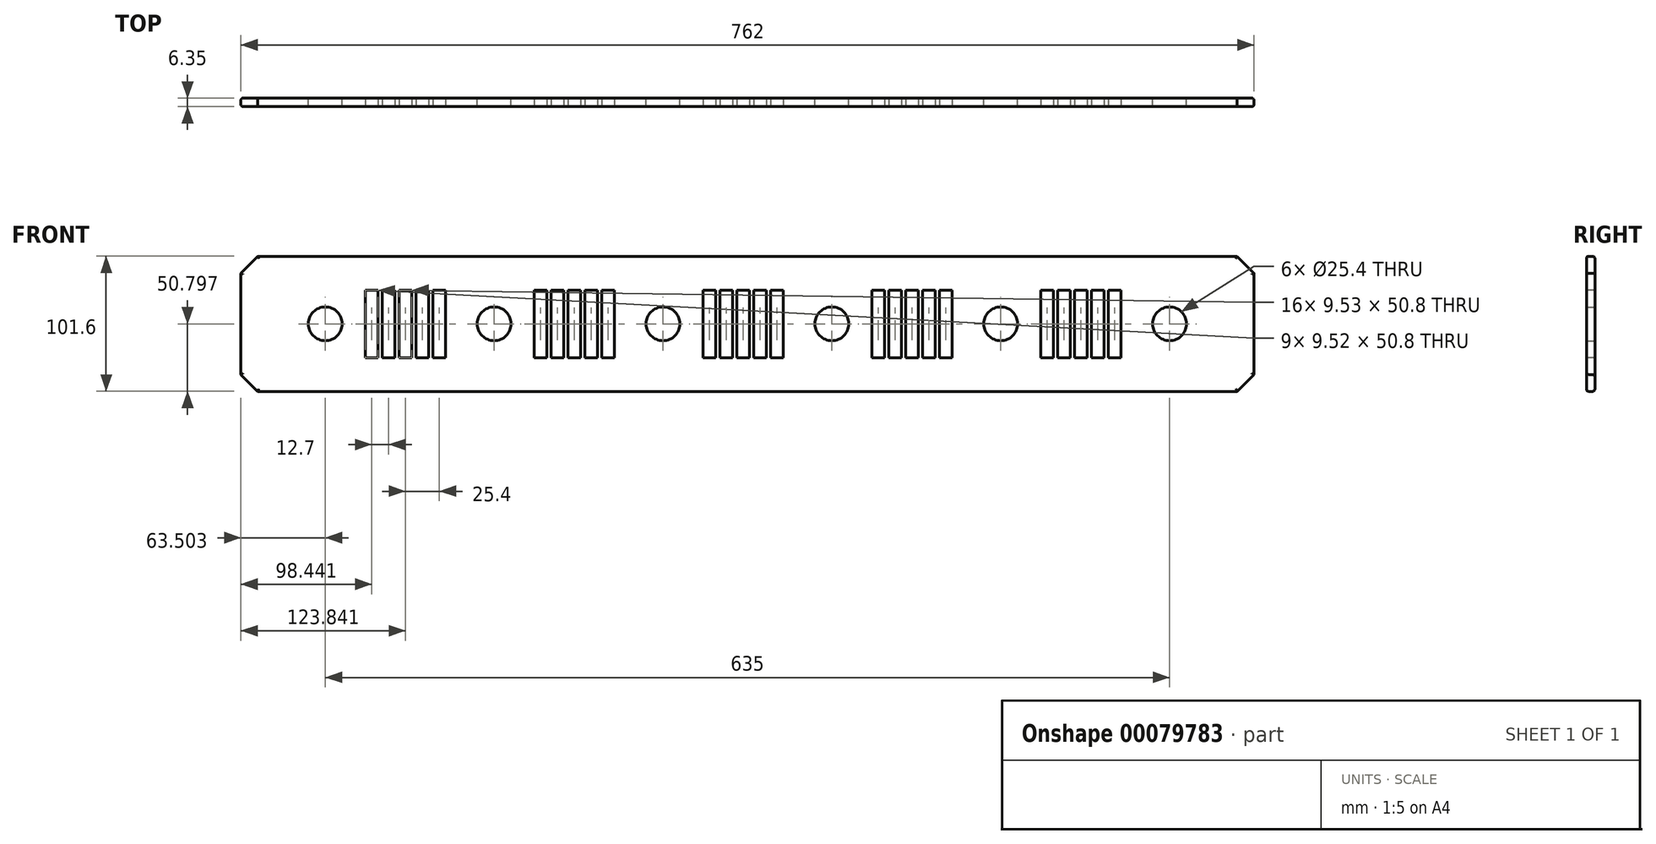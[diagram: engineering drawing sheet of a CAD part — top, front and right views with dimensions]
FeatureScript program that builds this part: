
annotation { "Feature Type Name" : "Feature", "Feature Type Description" : "" }
export const myFeature = defineFeature(function(context is Context, id is Id, definition is map)
    precondition{}
    {
        {
            var Q0;
            Q0=qCreatedBy(makeId("Front.planeOp"),FACE);
            var sketch = newSketch(context, id + "F0", { "sketchPlane" : qUnion([Q0])});
            skLineSegment(sketch, "E0.bottom", {"start": v(-378.92, -35.34) * mm, "end": v(383.08, -35.34) * mm});
            skLineSegment(sketch, "E0.top", {"start": v(-378.92, -136.94) * mm, "end": v(383.08, -136.94) * mm});
            skLineSegment(sketch, "E0.left", {"start": v(-378.92, -35.34) * mm, "end": v(-378.92, -136.94) * mm});
            skLineSegment(sketch, "E0.right", {"start": v(383.08, -35.34) * mm, "end": v(383.08, -136.94) * mm});
            skCircle(sketch, "E1", {"center": v(-315.42, -86.14) * mm, "radius": 12.7 * mm});
            skPoint(sketch, "E1.centerSnap0", {"position": v(-378.92, -86.14) * mm});
            skCircle(sketch, "E2", {"center": v(-188.42, -86.14) * mm, "radius": 12.7 * mm});
            skCircle(sketch, "E3", {"center": v(-61.42, -86.14) * mm, "radius": 12.7 * mm});
            skCircle(sketch, "E4", {"center": v(65.58, -86.14) * mm, "radius": 12.7 * mm});
            skCircle(sketch, "E5", {"center": v(192.58, -86.14) * mm, "radius": 12.7 * mm});
            skCircle(sketch, "E6", {"center": v(319.58, -86.14) * mm, "radius": 12.7 * mm});
            skSolve(sketch);
        }
        {
            var Q0;
            Q0=makeQuery(id+"F0.imprint","IMPRINT",FACE,{"disambiguationData":[TD([[makeQuery(id+"F0.imprint","IMPRINT",EDGE,{"derivedFrom":sQuery(id+"F0.wireOp",EDGE,"E0.bottom")}),-1.0]])]});
            extrude(context, id + "F1", {"entities" : qUnion([Q0]), "depth" : 6.35 * mm});
        }
        {
            var Q0;
            Q0=makeQuery(id+"F1.opExtrude","CAP_FACE",FACE,{"disambiguationData":[OSD([sQuery(id+"F0.wireOp",EDGE,"E0.bottom"),sQuery(id+"F0.wireOp",EDGE,"E0.top"),sQuery(id+"F0.wireOp",EDGE,"E0.left"),sQuery(id+"F0.wireOp",EDGE,"E0.right"),sQuery(id+"F0.wireOp",EDGE,"E1"),sQuery(id+"F0.wireOp",EDGE,"E2"),sQuery(id+"F0.wireOp",EDGE,"E3"),sQuery(id+"F0.wireOp",EDGE,"E4"),sQuery(id+"F0.wireOp",EDGE,"E5"),sQuery(id+"F0.wireOp",EDGE,"E6")])],"isStart":false});
            var sketch = newSketch(context, id + "F2", { "sketchPlane" : qUnion([Q0])});
            skLineSegment(sketch, "E7.bottom", {"start": v(-285.24, -60.74) * mm, "end": v(-275.72, -60.74) * mm});
            skLineSegment(sketch, "E7.top", {"start": v(-285.24, -111.54) * mm, "end": v(-275.72, -111.54) * mm});
            skLineSegment(sketch, "E7.left", {"start": v(-285.24, -60.74) * mm, "end": v(-285.24, -111.54) * mm});
            skLineSegment(sketch, "E7.right", {"start": v(-275.72, -60.74) * mm, "end": v(-275.72, -111.54) * mm});
            skLineSegment(sketch, "E8.1.0.0", {"start": v(-272.54, -60.74) * mm, "end": v(-263.02, -60.74) * mm});
            skLineSegment(sketch, "E8.1.0.1", {"start": v(-272.54, -111.54) * mm, "end": v(-263.02, -111.54) * mm});
            skLineSegment(sketch, "E8.1.0.2", {"start": v(-263.02, -60.74) * mm, "end": v(-263.02, -111.54) * mm});
            skLineSegment(sketch, "E8.1.0.3", {"start": v(-272.54, -60.74) * mm, "end": v(-272.54, -111.54) * mm});
            skLineSegment(sketch, "E8.2.0.0", {"start": v(-259.84, -60.74) * mm, "end": v(-250.32, -60.74) * mm});
            skLineSegment(sketch, "E8.2.0.1", {"start": v(-259.84, -111.54) * mm, "end": v(-250.32, -111.54) * mm});
            skLineSegment(sketch, "E8.2.0.2", {"start": v(-250.32, -60.74) * mm, "end": v(-250.32, -111.54) * mm});
            skLineSegment(sketch, "E8.2.0.3", {"start": v(-259.84, -60.74) * mm, "end": v(-259.84, -111.54) * mm});
            skLineSegment(sketch, "E8.3.0.0", {"start": v(-247.14, -60.74) * mm, "end": v(-237.62, -60.74) * mm});
            skLineSegment(sketch, "E8.3.0.1", {"start": v(-247.14, -111.54) * mm, "end": v(-237.62, -111.54) * mm});
            skLineSegment(sketch, "E8.3.0.2", {"start": v(-237.62, -60.74) * mm, "end": v(-237.62, -111.54) * mm});
            skLineSegment(sketch, "E8.3.0.3", {"start": v(-247.14, -60.74) * mm, "end": v(-247.14, -111.54) * mm});
            skLineSegment(sketch, "E8.4.0.0", {"start": v(-234.44, -60.74) * mm, "end": v(-224.92, -60.74) * mm});
            skLineSegment(sketch, "E8.4.0.1", {"start": v(-234.44, -111.54) * mm, "end": v(-224.92, -111.54) * mm});
            skLineSegment(sketch, "E8.4.0.2", {"start": v(-224.92, -60.74) * mm, "end": v(-224.92, -111.54) * mm});
            skLineSegment(sketch, "E8.4.0.3", {"start": v(-234.44, -60.74) * mm, "end": v(-234.44, -111.54) * mm});
            skLineSegment(sketch, "E8.direction1", {"start": v(-285.24, -60.74) * mm, "end": v(-272.54, -60.74) * mm, "construction": true});
            skLineSegment(sketch, "E9.bottom", {"start": v(-158.24, -60.74) * mm, "end": v(-148.72, -60.74) * mm});
            skLineSegment(sketch, "E9.top", {"start": v(-158.24, -111.54) * mm, "end": v(-148.72, -111.54) * mm});
            skLineSegment(sketch, "E9.left", {"start": v(-158.24, -60.74) * mm, "end": v(-158.24, -111.54) * mm});
            skLineSegment(sketch, "E9.right", {"start": v(-148.72, -60.74) * mm, "end": v(-148.72, -111.54) * mm});
            skLineSegment(sketch, "E10.1.0.0", {"start": v(-145.54, -60.74) * mm, "end": v(-136.02, -60.74) * mm});
            skLineSegment(sketch, "E10.1.0.1", {"start": v(-145.54, -111.54) * mm, "end": v(-136.02, -111.54) * mm});
            skLineSegment(sketch, "E10.1.0.2", {"start": v(-136.02, -60.74) * mm, "end": v(-136.02, -111.54) * mm});
            skLineSegment(sketch, "E10.1.0.3", {"start": v(-145.54, -60.74) * mm, "end": v(-145.54, -111.54) * mm});
            skLineSegment(sketch, "E10.2.0.0", {"start": v(-132.84, -60.74) * mm, "end": v(-123.32, -60.74) * mm});
            skLineSegment(sketch, "E10.2.0.1", {"start": v(-132.84, -111.54) * mm, "end": v(-123.32, -111.54) * mm});
            skLineSegment(sketch, "E10.2.0.2", {"start": v(-123.32, -60.74) * mm, "end": v(-123.32, -111.54) * mm});
            skLineSegment(sketch, "E10.2.0.3", {"start": v(-132.84, -60.74) * mm, "end": v(-132.84, -111.54) * mm});
            skLineSegment(sketch, "E10.3.0.0", {"start": v(-120.14, -60.74) * mm, "end": v(-110.62, -60.74) * mm});
            skLineSegment(sketch, "E10.3.0.1", {"start": v(-120.14, -111.54) * mm, "end": v(-110.62, -111.54) * mm});
            skLineSegment(sketch, "E10.3.0.2", {"start": v(-110.62, -60.74) * mm, "end": v(-110.62, -111.54) * mm});
            skLineSegment(sketch, "E10.3.0.3", {"start": v(-120.14, -60.74) * mm, "end": v(-120.14, -111.54) * mm});
            skLineSegment(sketch, "E10.4.0.0", {"start": v(-107.44, -60.74) * mm, "end": v(-97.92, -60.74) * mm});
            skLineSegment(sketch, "E10.4.0.1", {"start": v(-107.44, -111.54) * mm, "end": v(-97.92, -111.54) * mm});
            skLineSegment(sketch, "E10.4.0.2", {"start": v(-97.92, -60.74) * mm, "end": v(-97.92, -111.54) * mm});
            skLineSegment(sketch, "E10.4.0.3", {"start": v(-107.44, -60.74) * mm, "end": v(-107.44, -111.54) * mm});
            skLineSegment(sketch, "E10.direction1", {"start": v(-158.24, -60.74) * mm, "end": v(-145.54, -60.74) * mm, "construction": true});
            skLineSegment(sketch, "E11.bottom", {"start": v(-31.24, -60.74) * mm, "end": v(-21.72, -60.74) * mm});
            skLineSegment(sketch, "E11.top", {"start": v(-31.24, -111.54) * mm, "end": v(-21.72, -111.54) * mm});
            skLineSegment(sketch, "E11.left", {"start": v(-31.24, -60.74) * mm, "end": v(-31.24, -111.54) * mm});
            skLineSegment(sketch, "E11.right", {"start": v(-21.72, -60.74) * mm, "end": v(-21.72, -111.54) * mm});
            skLineSegment(sketch, "E12.1.0.0", {"start": v(-18.54, -60.74) * mm, "end": v(-9.02, -60.74) * mm});
            skLineSegment(sketch, "E12.1.0.1", {"start": v(-18.54, -111.54) * mm, "end": v(-9.02, -111.54) * mm});
            skLineSegment(sketch, "E12.1.0.2", {"start": v(-9.02, -60.74) * mm, "end": v(-9.02, -111.54) * mm});
            skLineSegment(sketch, "E12.1.0.3", {"start": v(-18.54, -60.74) * mm, "end": v(-18.54, -111.54) * mm});
            skLineSegment(sketch, "E12.2.0.0", {"start": v(-5.84, -60.74) * mm, "end": v(3.68, -60.74) * mm});
            skLineSegment(sketch, "E12.2.0.1", {"start": v(-5.84, -111.54) * mm, "end": v(3.68, -111.54) * mm});
            skLineSegment(sketch, "E12.2.0.2", {"start": v(3.68, -60.74) * mm, "end": v(3.68, -111.54) * mm});
            skLineSegment(sketch, "E12.2.0.3", {"start": v(-5.84, -60.74) * mm, "end": v(-5.84, -111.54) * mm});
            skLineSegment(sketch, "E12.3.0.0", {"start": v(6.86, -60.74) * mm, "end": v(16.38, -60.74) * mm});
            skLineSegment(sketch, "E12.3.0.1", {"start": v(6.86, -111.54) * mm, "end": v(16.38, -111.54) * mm});
            skLineSegment(sketch, "E12.3.0.2", {"start": v(16.38, -60.74) * mm, "end": v(16.38, -111.54) * mm});
            skLineSegment(sketch, "E12.3.0.3", {"start": v(6.86, -60.74) * mm, "end": v(6.86, -111.54) * mm});
            skLineSegment(sketch, "E12.4.0.0", {"start": v(19.56, -60.74) * mm, "end": v(29.08, -60.74) * mm});
            skLineSegment(sketch, "E12.4.0.1", {"start": v(19.56, -111.54) * mm, "end": v(29.08, -111.54) * mm});
            skLineSegment(sketch, "E12.4.0.2", {"start": v(29.08, -60.74) * mm, "end": v(29.08, -111.54) * mm});
            skLineSegment(sketch, "E12.4.0.3", {"start": v(19.56, -60.74) * mm, "end": v(19.56, -111.54) * mm});
            skLineSegment(sketch, "E12.direction1", {"start": v(-31.24, -60.74) * mm, "end": v(-18.54, -60.74) * mm, "construction": true});
            skLineSegment(sketch, "E13.bottom", {"start": v(95.76, -60.74) * mm, "end": v(105.28, -60.74) * mm});
            skLineSegment(sketch, "E13.top", {"start": v(95.76, -111.54) * mm, "end": v(105.28, -111.54) * mm});
            skLineSegment(sketch, "E13.left", {"start": v(95.76, -60.74) * mm, "end": v(95.76, -111.54) * mm});
            skLineSegment(sketch, "E13.right", {"start": v(105.28, -60.74) * mm, "end": v(105.28, -111.54) * mm});
            skLineSegment(sketch, "E14.1.0.0", {"start": v(108.46, -60.74) * mm, "end": v(117.98, -60.74) * mm});
            skLineSegment(sketch, "E14.1.0.1", {"start": v(108.46, -111.54) * mm, "end": v(117.98, -111.54) * mm});
            skLineSegment(sketch, "E14.1.0.2", {"start": v(117.98, -60.74) * mm, "end": v(117.98, -111.54) * mm});
            skLineSegment(sketch, "E14.1.0.3", {"start": v(108.46, -60.74) * mm, "end": v(108.46, -111.54) * mm});
            skLineSegment(sketch, "E14.2.0.0", {"start": v(121.16, -60.74) * mm, "end": v(130.68, -60.74) * mm});
            skLineSegment(sketch, "E14.2.0.1", {"start": v(121.16, -111.54) * mm, "end": v(130.68, -111.54) * mm});
            skLineSegment(sketch, "E14.2.0.2", {"start": v(130.68, -60.74) * mm, "end": v(130.68, -111.54) * mm});
            skLineSegment(sketch, "E14.2.0.3", {"start": v(121.16, -60.74) * mm, "end": v(121.16, -111.54) * mm});
            skLineSegment(sketch, "E14.3.0.0", {"start": v(133.86, -60.74) * mm, "end": v(143.38, -60.74) * mm});
            skLineSegment(sketch, "E14.3.0.1", {"start": v(133.86, -111.54) * mm, "end": v(143.38, -111.54) * mm});
            skLineSegment(sketch, "E14.3.0.2", {"start": v(143.38, -60.74) * mm, "end": v(143.38, -111.54) * mm});
            skLineSegment(sketch, "E14.3.0.3", {"start": v(133.86, -60.74) * mm, "end": v(133.86, -111.54) * mm});
            skLineSegment(sketch, "E14.4.0.0", {"start": v(146.56, -60.74) * mm, "end": v(156.08, -60.74) * mm});
            skLineSegment(sketch, "E14.4.0.1", {"start": v(146.56, -111.54) * mm, "end": v(156.08, -111.54) * mm});
            skLineSegment(sketch, "E14.4.0.2", {"start": v(156.08, -60.74) * mm, "end": v(156.08, -111.54) * mm});
            skLineSegment(sketch, "E14.4.0.3", {"start": v(146.56, -60.74) * mm, "end": v(146.56, -111.54) * mm});
            skLineSegment(sketch, "E14.direction1", {"start": v(95.76, -60.74) * mm, "end": v(108.46, -60.74) * mm, "construction": true});
            skLineSegment(sketch, "E15.bottom", {"start": v(222.76, -60.74) * mm, "end": v(232.28, -60.74) * mm});
            skLineSegment(sketch, "E15.top", {"start": v(222.76, -111.54) * mm, "end": v(232.28, -111.54) * mm});
            skLineSegment(sketch, "E15.left", {"start": v(222.76, -60.74) * mm, "end": v(222.76, -111.54) * mm});
            skLineSegment(sketch, "E15.right", {"start": v(232.28, -60.74) * mm, "end": v(232.28, -111.54) * mm});
            skLineSegment(sketch, "E16.1.0.0", {"start": v(235.46, -60.74) * mm, "end": v(244.98, -60.74) * mm});
            skLineSegment(sketch, "E16.1.0.1", {"start": v(235.46, -111.54) * mm, "end": v(244.98, -111.54) * mm});
            skLineSegment(sketch, "E16.1.0.2", {"start": v(244.98, -60.74) * mm, "end": v(244.98, -111.54) * mm});
            skLineSegment(sketch, "E16.1.0.3", {"start": v(235.46, -60.74) * mm, "end": v(235.46, -111.54) * mm});
            skLineSegment(sketch, "E16.2.0.0", {"start": v(248.16, -60.74) * mm, "end": v(257.68, -60.74) * mm});
            skLineSegment(sketch, "E16.2.0.1", {"start": v(248.16, -111.54) * mm, "end": v(257.68, -111.54) * mm});
            skLineSegment(sketch, "E16.2.0.2", {"start": v(257.68, -60.74) * mm, "end": v(257.68, -111.54) * mm});
            skLineSegment(sketch, "E16.2.0.3", {"start": v(248.16, -60.74) * mm, "end": v(248.16, -111.54) * mm});
            skLineSegment(sketch, "E16.3.0.0", {"start": v(260.86, -60.74) * mm, "end": v(270.38, -60.74) * mm});
            skLineSegment(sketch, "E16.3.0.1", {"start": v(260.86, -111.54) * mm, "end": v(270.38, -111.54) * mm});
            skLineSegment(sketch, "E16.3.0.2", {"start": v(270.38, -60.74) * mm, "end": v(270.38, -111.54) * mm});
            skLineSegment(sketch, "E16.3.0.3", {"start": v(260.86, -60.74) * mm, "end": v(260.86, -111.54) * mm});
            skLineSegment(sketch, "E16.4.0.0", {"start": v(273.56, -60.74) * mm, "end": v(283.08, -60.74) * mm});
            skLineSegment(sketch, "E16.4.0.1", {"start": v(273.56, -111.54) * mm, "end": v(283.08, -111.54) * mm});
            skLineSegment(sketch, "E16.4.0.2", {"start": v(283.08, -60.74) * mm, "end": v(283.08, -111.54) * mm});
            skLineSegment(sketch, "E16.4.0.3", {"start": v(273.56, -60.74) * mm, "end": v(273.56, -111.54) * mm});
            skLineSegment(sketch, "E16.direction1", {"start": v(222.76, -60.74) * mm, "end": v(235.46, -60.74) * mm, "construction": true});
            skSolve(sketch);
        }
        {
            var Q0;
            Q0 = qSketchRegion(id + "F2", true);
            extrude(context, id + "F3", {"entities" : qUnion([Q0]), "operationType" : NewBodyOperationType.REMOVE, "oppositeDirection" : true, "depth" : 25.4 * mm});
        }
        {
            var Q0;
            Q0=makeQuery(id+"F1.opExtrude","SWEPT_EDGE",EDGE,{"disambiguationData":[OSD([sQuery(id+"F0.wireOp",EDGE,"E0.bottom"),sQuery(id+"F0.wireOp",EDGE,"E0.left")])]});
            var Q1;
            Q1=makeQuery(id+"F1.opExtrude","SWEPT_EDGE",EDGE,{"disambiguationData":[OSD([sQuery(id+"F0.wireOp",EDGE,"E0.top"),sQuery(id+"F0.wireOp",EDGE,"E0.left")])]});
            var Q2;
            Q2=makeQuery(id+"F1.opExtrude","SWEPT_EDGE",EDGE,{"disambiguationData":[OSD([sQuery(id+"F0.wireOp",EDGE,"E0.top"),sQuery(id+"F0.wireOp",EDGE,"E0.right")])]});
            var Q3;
            Q3=makeQuery(id+"F1.opExtrude","SWEPT_EDGE",EDGE,{"disambiguationData":[OSD([sQuery(id+"F0.wireOp",EDGE,"E0.bottom"),sQuery(id+"F0.wireOp",EDGE,"E0.right")])]});
            chamfer(context, id + "F4", {"entities" : qUnion([Q0, Q1, Q2, Q3]), "width" : 12.7 * mm, "tangentPropagation" : true});
        }
        {
            var Q0;
            Q0=makeQuery(id+"F1.opExtrude","CAP_EDGE",EDGE,{"disambiguationData":[OSD([sQuery(id+"F0.wireOp",EDGE,"E0.bottom")])],"isStart":false});
            var Q1;
            Q1=makeQuery(id+"F1.opExtrude","CAP_EDGE",EDGE,{"disambiguationData":[OSD([sQuery(id+"F0.wireOp",EDGE,"E0.bottom")])],"isStart":true});
            var Q2;
            {var subQ0=sQuery(id+"F0.wireOp",EDGE,"E0.left");var subQ1=sQuery(id+"F0.wireOp",EDGE,"E0.bottom");Q2=makeQuery(id+"F4.opChamfer","BLEND_EDGE",EDGE,{"blendedFrom":[makeQuery(id+"F1.opExtrude","SWEPT_EDGE",EDGE,{"disambiguationData":[OSD([subQ1,subQ0])]}),makeQuery(id+"F1.opExtrude","CAP_FACE",FACE,{"disambiguationData":[OSD([subQ1,sQuery(id+"F0.wireOp",EDGE,"E0.top"),subQ0,sQuery(id+"F0.wireOp",EDGE,"E0.right"),sQuery(id+"F0.wireOp",EDGE,"E1"),sQuery(id+"F0.wireOp",EDGE,"E2"),sQuery(id+"F0.wireOp",EDGE,"E3"),sQuery(id+"F0.wireOp",EDGE,"E4"),sQuery(id+"F0.wireOp",EDGE,"E5"),sQuery(id+"F0.wireOp",EDGE,"E6")])],"isStart":false})],"blendedInto":[makeQuery(id+"F1.opExtrude","CAP_FACE",FACE,{"disambiguationData":[OSD([subQ1,sQuery(id+"F0.wireOp",EDGE,"E0.top"),subQ0,sQuery(id+"F0.wireOp",EDGE,"E0.right"),sQuery(id+"F0.wireOp",EDGE,"E1"),sQuery(id+"F0.wireOp",EDGE,"E2"),sQuery(id+"F0.wireOp",EDGE,"E3"),sQuery(id+"F0.wireOp",EDGE,"E4"),sQuery(id+"F0.wireOp",EDGE,"E5"),sQuery(id+"F0.wireOp",EDGE,"E6")])],"isStart":false})]});}
            var Q3;
            {var subQ0=sQuery(id+"F0.wireOp",EDGE,"E0.left");var subQ1=sQuery(id+"F0.wireOp",EDGE,"E0.bottom");Q3=makeQuery(id+"F4.opChamfer","BLEND_EDGE",EDGE,{"blendedFrom":[makeQuery(id+"F1.opExtrude","SWEPT_EDGE",EDGE,{"disambiguationData":[OSD([subQ1,subQ0])]}),makeQuery(id+"F1.opExtrude","CAP_FACE",FACE,{"disambiguationData":[OSD([subQ1,sQuery(id+"F0.wireOp",EDGE,"E0.top"),subQ0,sQuery(id+"F0.wireOp",EDGE,"E0.right"),sQuery(id+"F0.wireOp",EDGE,"E1"),sQuery(id+"F0.wireOp",EDGE,"E2"),sQuery(id+"F0.wireOp",EDGE,"E3"),sQuery(id+"F0.wireOp",EDGE,"E4"),sQuery(id+"F0.wireOp",EDGE,"E5"),sQuery(id+"F0.wireOp",EDGE,"E6")])],"isStart":true})],"blendedInto":[makeQuery(id+"F1.opExtrude","CAP_FACE",FACE,{"disambiguationData":[OSD([subQ1,sQuery(id+"F0.wireOp",EDGE,"E0.top"),subQ0,sQuery(id+"F0.wireOp",EDGE,"E0.right"),sQuery(id+"F0.wireOp",EDGE,"E1"),sQuery(id+"F0.wireOp",EDGE,"E2"),sQuery(id+"F0.wireOp",EDGE,"E3"),sQuery(id+"F0.wireOp",EDGE,"E4"),sQuery(id+"F0.wireOp",EDGE,"E5"),sQuery(id+"F0.wireOp",EDGE,"E6")])],"isStart":true})]});}
            var Q4;
            Q4=makeQuery(id+"F1.opExtrude","CAP_EDGE",EDGE,{"disambiguationData":[OSD([sQuery(id+"F0.wireOp",EDGE,"E0.left")])],"isStart":false});
            var Q5;
            Q5=makeQuery(id+"F1.opExtrude","CAP_EDGE",EDGE,{"disambiguationData":[OSD([sQuery(id+"F0.wireOp",EDGE,"E0.left")])],"isStart":true});
            var Q6;
            {var subQ0=sQuery(id+"F0.wireOp",EDGE,"E0.left");var subQ1=sQuery(id+"F0.wireOp",EDGE,"E0.top");Q6=makeQuery(id+"F4.opChamfer","BLEND_EDGE",EDGE,{"blendedFrom":[makeQuery(id+"F1.opExtrude","SWEPT_EDGE",EDGE,{"disambiguationData":[OSD([subQ1,subQ0])]}),makeQuery(id+"F1.opExtrude","CAP_FACE",FACE,{"disambiguationData":[OSD([sQuery(id+"F0.wireOp",EDGE,"E0.bottom"),subQ1,subQ0,sQuery(id+"F0.wireOp",EDGE,"E0.right"),sQuery(id+"F0.wireOp",EDGE,"E1"),sQuery(id+"F0.wireOp",EDGE,"E2"),sQuery(id+"F0.wireOp",EDGE,"E3"),sQuery(id+"F0.wireOp",EDGE,"E4"),sQuery(id+"F0.wireOp",EDGE,"E5"),sQuery(id+"F0.wireOp",EDGE,"E6")])],"isStart":false})],"blendedInto":[makeQuery(id+"F1.opExtrude","CAP_FACE",FACE,{"disambiguationData":[OSD([sQuery(id+"F0.wireOp",EDGE,"E0.bottom"),subQ1,subQ0,sQuery(id+"F0.wireOp",EDGE,"E0.right"),sQuery(id+"F0.wireOp",EDGE,"E1"),sQuery(id+"F0.wireOp",EDGE,"E2"),sQuery(id+"F0.wireOp",EDGE,"E3"),sQuery(id+"F0.wireOp",EDGE,"E4"),sQuery(id+"F0.wireOp",EDGE,"E5"),sQuery(id+"F0.wireOp",EDGE,"E6")])],"isStart":false})]});}
            var Q7;
            {var subQ0=sQuery(id+"F0.wireOp",EDGE,"E0.left");var subQ1=sQuery(id+"F0.wireOp",EDGE,"E0.top");Q7=makeQuery(id+"F4.opChamfer","BLEND_EDGE",EDGE,{"blendedFrom":[makeQuery(id+"F1.opExtrude","SWEPT_EDGE",EDGE,{"disambiguationData":[OSD([subQ1,subQ0])]}),makeQuery(id+"F1.opExtrude","CAP_FACE",FACE,{"disambiguationData":[OSD([sQuery(id+"F0.wireOp",EDGE,"E0.bottom"),subQ1,subQ0,sQuery(id+"F0.wireOp",EDGE,"E0.right"),sQuery(id+"F0.wireOp",EDGE,"E1"),sQuery(id+"F0.wireOp",EDGE,"E2"),sQuery(id+"F0.wireOp",EDGE,"E3"),sQuery(id+"F0.wireOp",EDGE,"E4"),sQuery(id+"F0.wireOp",EDGE,"E5"),sQuery(id+"F0.wireOp",EDGE,"E6")])],"isStart":true})],"blendedInto":[makeQuery(id+"F1.opExtrude","CAP_FACE",FACE,{"disambiguationData":[OSD([sQuery(id+"F0.wireOp",EDGE,"E0.bottom"),subQ1,subQ0,sQuery(id+"F0.wireOp",EDGE,"E0.right"),sQuery(id+"F0.wireOp",EDGE,"E1"),sQuery(id+"F0.wireOp",EDGE,"E2"),sQuery(id+"F0.wireOp",EDGE,"E3"),sQuery(id+"F0.wireOp",EDGE,"E4"),sQuery(id+"F0.wireOp",EDGE,"E5"),sQuery(id+"F0.wireOp",EDGE,"E6")])],"isStart":true})]});}
            var Q8;
            {var subQ0=sQuery(id+"F0.wireOp",EDGE,"E0.right");var subQ1=sQuery(id+"F0.wireOp",EDGE,"E0.bottom");Q8=makeQuery(id+"F4.opChamfer","BLEND_EDGE",EDGE,{"blendedFrom":[makeQuery(id+"F1.opExtrude","SWEPT_EDGE",EDGE,{"disambiguationData":[OSD([subQ1,subQ0])]}),makeQuery(id+"F1.opExtrude","CAP_FACE",FACE,{"disambiguationData":[OSD([subQ1,sQuery(id+"F0.wireOp",EDGE,"E0.top"),sQuery(id+"F0.wireOp",EDGE,"E0.left"),subQ0,sQuery(id+"F0.wireOp",EDGE,"E1"),sQuery(id+"F0.wireOp",EDGE,"E2"),sQuery(id+"F0.wireOp",EDGE,"E3"),sQuery(id+"F0.wireOp",EDGE,"E4"),sQuery(id+"F0.wireOp",EDGE,"E5"),sQuery(id+"F0.wireOp",EDGE,"E6")])],"isStart":true})],"blendedInto":[makeQuery(id+"F1.opExtrude","CAP_FACE",FACE,{"disambiguationData":[OSD([subQ1,sQuery(id+"F0.wireOp",EDGE,"E0.top"),sQuery(id+"F0.wireOp",EDGE,"E0.left"),subQ0,sQuery(id+"F0.wireOp",EDGE,"E1"),sQuery(id+"F0.wireOp",EDGE,"E2"),sQuery(id+"F0.wireOp",EDGE,"E3"),sQuery(id+"F0.wireOp",EDGE,"E4"),sQuery(id+"F0.wireOp",EDGE,"E5"),sQuery(id+"F0.wireOp",EDGE,"E6")])],"isStart":true})]});}
            var Q9;
            {var subQ0=sQuery(id+"F0.wireOp",EDGE,"E0.right");var subQ1=sQuery(id+"F0.wireOp",EDGE,"E0.bottom");Q9=makeQuery(id+"F4.opChamfer","BLEND_EDGE",EDGE,{"blendedFrom":[makeQuery(id+"F1.opExtrude","SWEPT_EDGE",EDGE,{"disambiguationData":[OSD([subQ1,subQ0])]}),makeQuery(id+"F1.opExtrude","CAP_FACE",FACE,{"disambiguationData":[OSD([subQ1,sQuery(id+"F0.wireOp",EDGE,"E0.top"),sQuery(id+"F0.wireOp",EDGE,"E0.left"),subQ0,sQuery(id+"F0.wireOp",EDGE,"E1"),sQuery(id+"F0.wireOp",EDGE,"E2"),sQuery(id+"F0.wireOp",EDGE,"E3"),sQuery(id+"F0.wireOp",EDGE,"E4"),sQuery(id+"F0.wireOp",EDGE,"E5"),sQuery(id+"F0.wireOp",EDGE,"E6")])],"isStart":false})],"blendedInto":[makeQuery(id+"F1.opExtrude","CAP_FACE",FACE,{"disambiguationData":[OSD([subQ1,sQuery(id+"F0.wireOp",EDGE,"E0.top"),sQuery(id+"F0.wireOp",EDGE,"E0.left"),subQ0,sQuery(id+"F0.wireOp",EDGE,"E1"),sQuery(id+"F0.wireOp",EDGE,"E2"),sQuery(id+"F0.wireOp",EDGE,"E3"),sQuery(id+"F0.wireOp",EDGE,"E4"),sQuery(id+"F0.wireOp",EDGE,"E5"),sQuery(id+"F0.wireOp",EDGE,"E6")])],"isStart":false})]});}
            var Q10;
            Q10=makeQuery(id+"F1.opExtrude","CAP_EDGE",EDGE,{"disambiguationData":[OSD([sQuery(id+"F0.wireOp",EDGE,"E0.right")])],"isStart":true});
            var Q11;
            Q11=makeQuery(id+"F1.opExtrude","CAP_EDGE",EDGE,{"disambiguationData":[OSD([sQuery(id+"F0.wireOp",EDGE,"E0.right")])],"isStart":false});
            var Q12;
            {var subQ0=sQuery(id+"F0.wireOp",EDGE,"E0.right");var subQ1=sQuery(id+"F0.wireOp",EDGE,"E0.top");Q12=makeQuery(id+"F4.opChamfer","BLEND_EDGE",EDGE,{"blendedFrom":[makeQuery(id+"F1.opExtrude","SWEPT_EDGE",EDGE,{"disambiguationData":[OSD([subQ1,subQ0])]}),makeQuery(id+"F1.opExtrude","CAP_FACE",FACE,{"disambiguationData":[OSD([sQuery(id+"F0.wireOp",EDGE,"E0.bottom"),subQ1,sQuery(id+"F0.wireOp",EDGE,"E0.left"),subQ0,sQuery(id+"F0.wireOp",EDGE,"E1"),sQuery(id+"F0.wireOp",EDGE,"E2"),sQuery(id+"F0.wireOp",EDGE,"E3"),sQuery(id+"F0.wireOp",EDGE,"E4"),sQuery(id+"F0.wireOp",EDGE,"E5"),sQuery(id+"F0.wireOp",EDGE,"E6")])],"isStart":false})],"blendedInto":[makeQuery(id+"F1.opExtrude","CAP_FACE",FACE,{"disambiguationData":[OSD([sQuery(id+"F0.wireOp",EDGE,"E0.bottom"),subQ1,sQuery(id+"F0.wireOp",EDGE,"E0.left"),subQ0,sQuery(id+"F0.wireOp",EDGE,"E1"),sQuery(id+"F0.wireOp",EDGE,"E2"),sQuery(id+"F0.wireOp",EDGE,"E3"),sQuery(id+"F0.wireOp",EDGE,"E4"),sQuery(id+"F0.wireOp",EDGE,"E5"),sQuery(id+"F0.wireOp",EDGE,"E6")])],"isStart":false})]});}
            var Q13;
            Q13=makeQuery(id+"F1.opExtrude","CAP_EDGE",EDGE,{"disambiguationData":[OSD([sQuery(id+"F0.wireOp",EDGE,"E0.top")])],"isStart":true});
            var Q14;
            Q14=makeQuery(id+"F1.opExtrude","CAP_EDGE",EDGE,{"disambiguationData":[OSD([sQuery(id+"F0.wireOp",EDGE,"E0.top")])],"isStart":false});
            fillet(context, id + "F5", {"entities" : qUnion([Q0, Q1, Q2, Q3, Q4, Q5, Q6, Q7, Q8, Q9, Q10, Q11, Q12, Q13, Q14]), "radius" : 1.6 * mm, "tangentPropagation" : true, "allowEdgeOverflow" : false});
        }
    });
